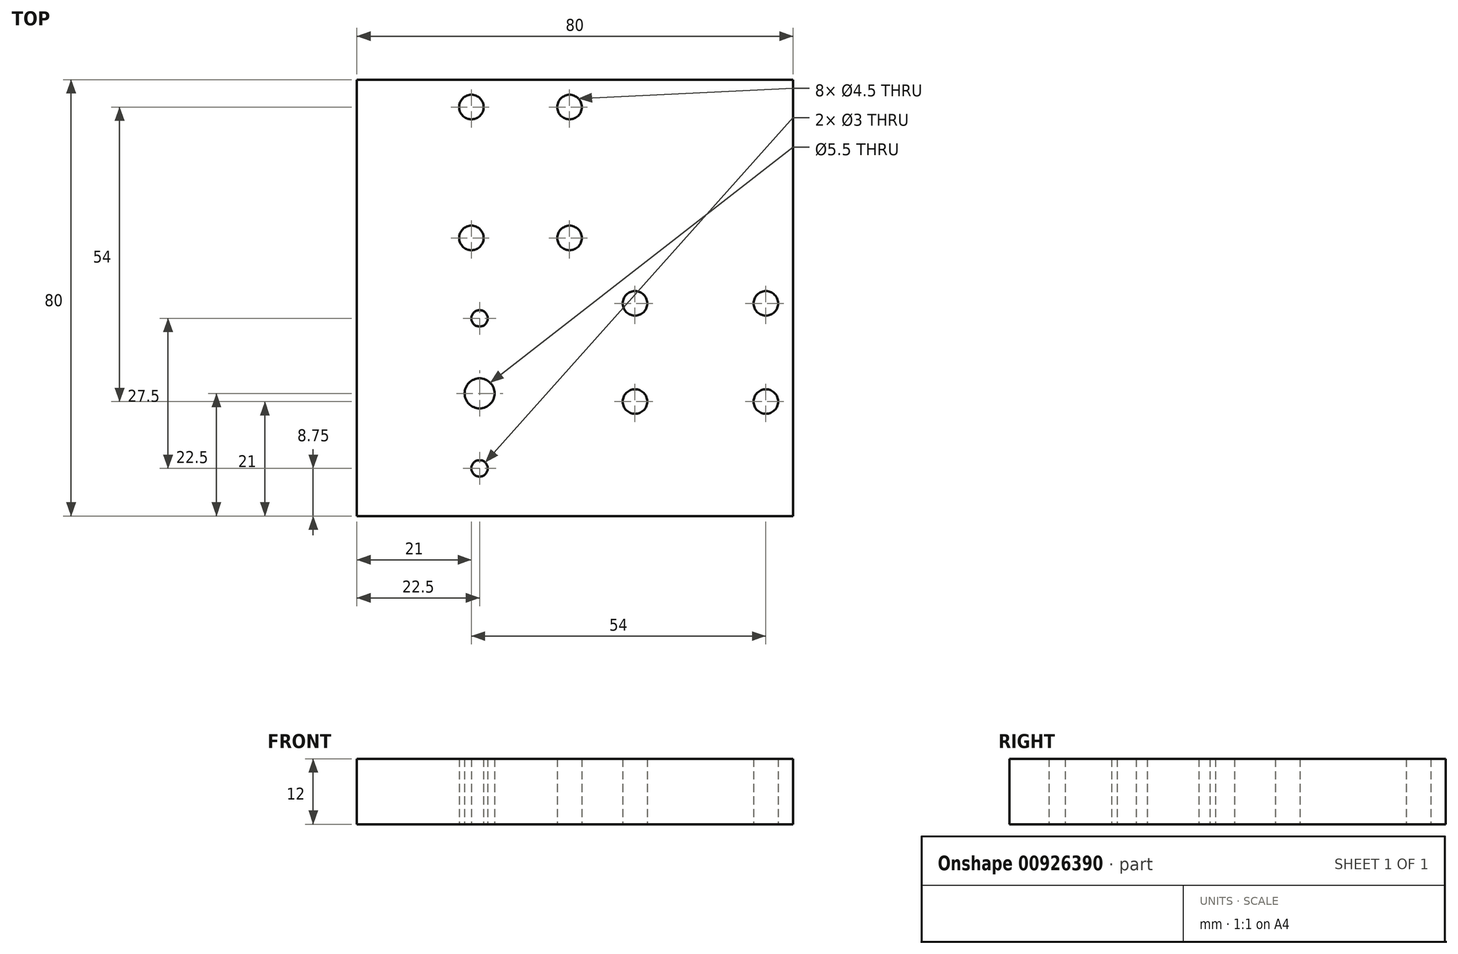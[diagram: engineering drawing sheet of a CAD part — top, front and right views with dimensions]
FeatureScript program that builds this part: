
annotation { "Feature Type Name" : "Feature", "Feature Type Description" : "" }
export const myFeature = defineFeature(function(context is Context, id is Id, definition is map)
    precondition{}
    {
        {
            var Q0;
            Q0=qCreatedBy(makeId("Top.planeOp"),FACE);
            var sketch = newSketch(context, id + "F0", { "sketchPlane" : qUnion([Q0])});
            skLineSegment(sketch, "E0.bottom", {"start": v(0, 0) * mm, "end": v(80, 0) * mm});
            skLineSegment(sketch, "E0.top", {"start": v(0, 80) * mm, "end": v(80, 80) * mm});
            skLineSegment(sketch, "E0.left", {"start": v(0, 0) * mm, "end": v(0, 80) * mm});
            skLineSegment(sketch, "E0.right", {"start": v(80, 0) * mm, "end": v(80, 80) * mm});
            skCircle(sketch, "E1", {"center": v(51, 39) * mm, "radius": 2.25 * mm});
            skCircle(sketch, "E2", {"center": v(75, 39) * mm, "radius": 2.25 * mm});
            skCircle(sketch, "E3", {"center": v(51, 21) * mm, "radius": 2.25 * mm});
            skCircle(sketch, "E4", {"center": v(75, 21) * mm, "radius": 2.25 * mm});
            skCircle(sketch, "E5", {"center": v(22.5, 8.75) * mm, "radius": 1.5 * mm});
            skCircle(sketch, "E6", {"center": v(22.5, 22.5) * mm, "radius": 2.75 * mm});
            skCircle(sketch, "E7", {"center": v(22.5, 36.25) * mm, "radius": 1.5 * mm});
            skLineSegment(sketch, "E8", {"start": v(22.5, 80) * mm, "end": v(22.5, 0) * mm, "construction": true});
            skLineSegment(sketch, "E9", {"start": v(80, 80) * mm, "end": v(0, 0) * mm, "construction": true});
            skLineSegment(sketch, "E10.bottom", {"start": v(51, 39) * mm, "end": v(75, 39) * mm, "construction": true});
            skLineSegment(sketch, "E10.top", {"start": v(51, 21) * mm, "end": v(75, 21) * mm, "construction": true});
            skLineSegment(sketch, "E10.left", {"start": v(51, 39) * mm, "end": v(51, 21) * mm, "construction": true});
            skLineSegment(sketch, "E10.right", {"start": v(75, 39) * mm, "end": v(75, 21) * mm, "construction": true});
            skCircle(sketch, "E11.MirrorC", {"center": v(21, 75) * mm, "radius": 2.25 * mm});
            skLineSegment(sketch, "E12.MirrorCS", {"start": v(39, 75) * mm, "end": v(21, 75) * mm, "construction": true});
            skLineSegment(sketch, "E13.MirrorCS", {"start": v(39, 51) * mm, "end": v(39, 75) * mm, "construction": true});
            skLineSegment(sketch, "E14.MirrorCS", {"start": v(21, 51) * mm, "end": v(21, 75) * mm, "construction": true});
            skCircle(sketch, "E15.MirrorC", {"center": v(39, 75) * mm, "radius": 2.25 * mm});
            skCircle(sketch, "E16.MirrorC", {"center": v(39, 51) * mm, "radius": 2.25 * mm});
            skLineSegment(sketch, "E17.MirrorCS", {"start": v(39, 51) * mm, "end": v(21, 51) * mm, "construction": true});
            skCircle(sketch, "E18.MirrorC", {"center": v(21, 51) * mm, "radius": 2.25 * mm});
            skSolve(sketch);
        }
        {
            var Q0;
            Q0=makeQuery(id+"F0.imprint","IMPRINT",FACE,{"disambiguationData":[TD([[makeQuery(id+"F0.imprint","IMPRINT",EDGE,{"derivedFrom":sQuery(id+"F0.wireOp",EDGE,"E0.bottom")}),1.0]])]});
            var Q1;
            Q1 = qConstructionFilter(qBodyType(qCreatedBy(id + "F0" ,EDGE), BodyType.WIRE), ConstructionObject.NO);
            extrude(context, id + "F1", {"entities" : qUnion([Q0]), "surfaceEntities" : qUnion([Q1]), "depth" : 12 * mm, "offsetDistance" : 25 * mm});
        }
    });
